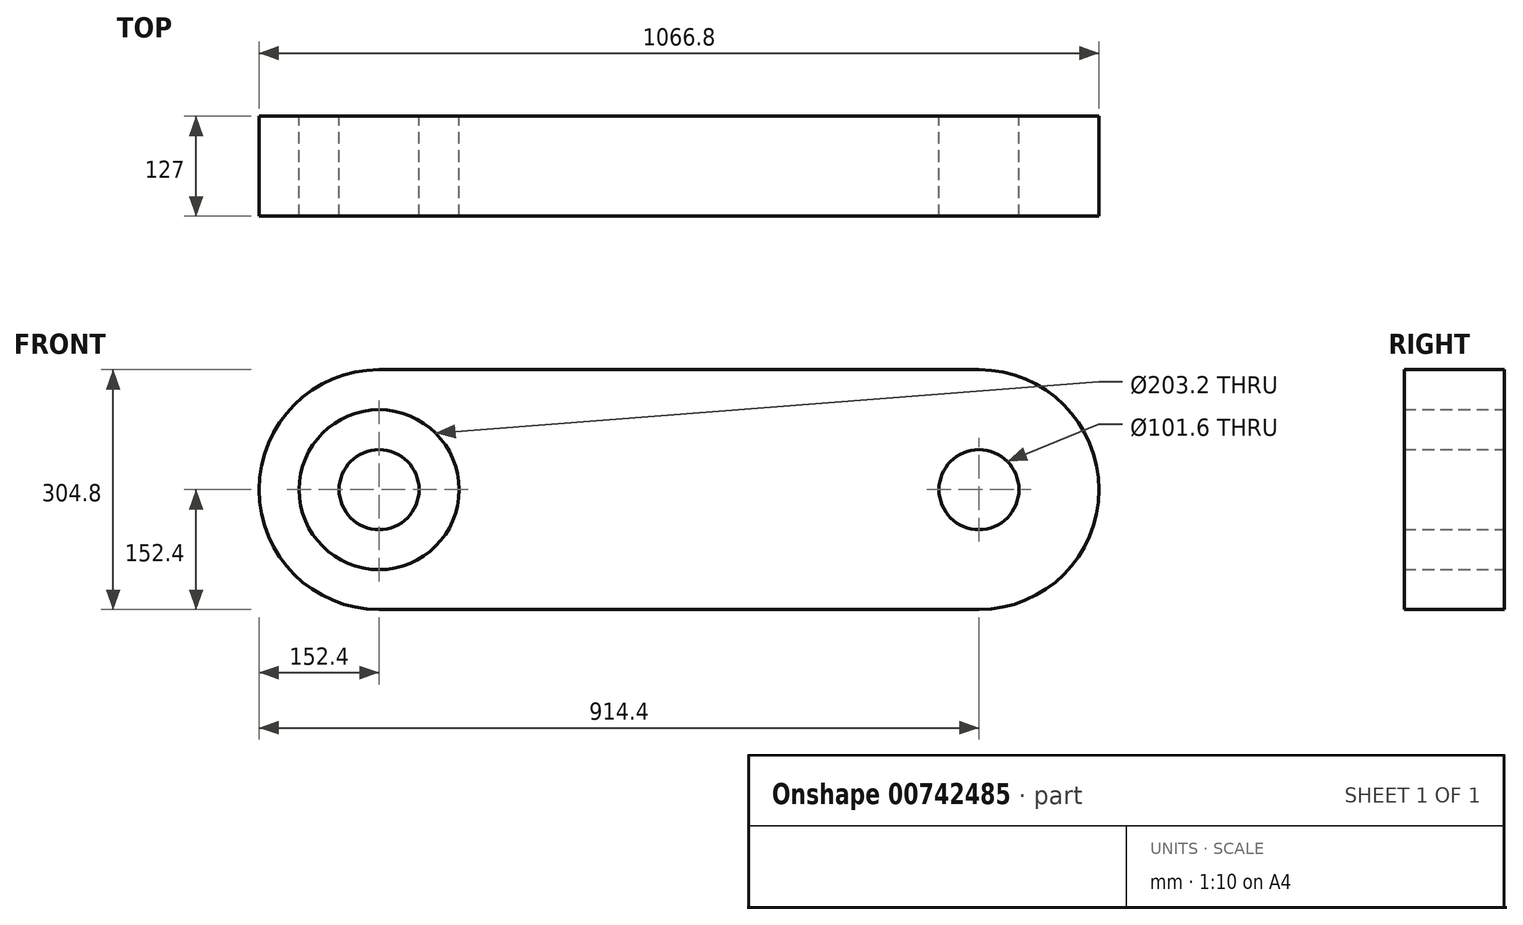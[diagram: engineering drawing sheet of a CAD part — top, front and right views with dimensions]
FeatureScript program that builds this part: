
annotation { "Feature Type Name" : "Feature", "Feature Type Description" : "" }
export const myFeature = defineFeature(function(context is Context, id is Id, definition is map)
    precondition{}
    {
        {
            var Q0;
            Q0=qCreatedBy(makeId("Front.planeOp"),FACE);
            var sketch = newSketch(context, id + "F0", { "sketchPlane" : qUnion([Q0])});
            skCircle(sketch, "E0", {"center": v(-381, 0) * mm, "radius": 50.8 * mm});
            skCircle(sketch, "E1", {"center": v(-381, 0) * mm, "radius": 101.6 * mm});
            skCircle(sketch, "E2", {"center": v(-381, 0) * mm, "radius": 152.4 * mm});
            skLineSegment(sketch, "E3", {"start": v(-381, 152.4) * mm, "end": v(0, 152.4) * mm});
            skLineSegment(sketch, "E4.MirrorCS", {"start": v(-381, -152.4) * mm, "end": v(0, -152.4) * mm});
            skCircle(sketch, "E5.MirrorC", {"center": v(381, 0) * mm, "radius": 152.4 * mm});
            skCircle(sketch, "E6.MirrorC", {"center": v(381, 0) * mm, "radius": 101.6 * mm});
            skLineSegment(sketch, "E7.MirrorCS", {"start": v(381, 152.4) * mm, "end": v(0, 152.4) * mm});
            skCircle(sketch, "E8.MirrorC", {"center": v(381, 0) * mm, "radius": 50.8 * mm});
            skLineSegment(sketch, "E9.MirrorCS", {"start": v(381, -152.4) * mm, "end": v(0, -152.4) * mm});
            skSolve(sketch);
        }
        {
            var Q0;
            Q0 = qSketchRegion(id + "F0", true);
            var Q1;
            Q1=makeQuery(id+"F0.imprint","IMPRINT",FACE,{"disambiguationData":[TD([[makeQuery(id+"F0.imprint","IMPRINT",EDGE,{"derivedFrom":sQuery(id+"F0.wireOp",EDGE,"E0")}),1.0]])]});
            var Q2;
            Q2=makeQuery(id+"F0.imprint","IMPRINT",FACE,{"disambiguationData":[TD([[makeQuery(id+"F0.imprint","IMPRINT",EDGE,{"derivedFrom":sQuery(id+"F0.wireOp",EDGE,"E8.MirrorC")}),-1.0]])]});
            extrude(context, id + "F1", {"entities" : qUnion([Q0, Q1, Q2]), "endBound" : BoundingType.SYMMETRIC, "depth" : 127 * mm, "offsetDistance" : 25.4 * mm});
        }
    });
